# Revit family: Zumtobel PANOS INF PWH
name_source: partatom
category: Lighting Fixtures
revit_build: Autodesk Revit 2015 (Build: 20160512_1515(x64)
units: mm (PartAtom-declared; Revit-internal decimal feet)

## types (2) — shared parameters
Assembly Code = D5020200
Color Filter = 16777215
Description = LED luminaire
Dimming Lamp Color Temperature Shift = <None>
Emit Shape Visible in Rendering = No
Lamp = LED
Manufacturer = Zumtobel Lighting
Tilt Angle = -90.00°
URL = http://www.zumtobel.com
Voltage = 230 V
zero-valued in all types: Default Elevation

## per-type parameters (varying)
| type | Apparent Load | Emit from Circle Diameter | Height | Length | Model | Photometric Web File | Width |
| PANOS INF PWH R70 | 12 VA | 56 mm  [stored 0.183727 ft] | 227 mm  [stored 0.744751 ft] | 70 mm  [stored 0.229659 ft] | 60510393 | ST9371.IES | 70 mm  [stored 0.229659 ft] |
| PANOS INF PWH R100 | 22 VA | 85 mm  [stored 0.278871 ft] | 276 mm  [stored 0.905512 ft] | 100 mm  [stored 0.328084 ft] | 60510429 | ST9392.IES | 100 mm  [stored 0.328084 ft] |

note: [stored X ft] marks values corroborated as IEEE doubles in the binary element streams (Revit-internal decimal feet)

## geometry (parser evidence)
native form markers: Blend x14, Sweep x2
no freeform markers — native parametric forms only
